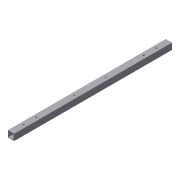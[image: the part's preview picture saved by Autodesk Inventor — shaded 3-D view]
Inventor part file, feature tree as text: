
AUTODESK INVENTOR PART (.ipt)
format: ipt  version: 2012 (Build 160160000, 160)  size: 108,544 bytes
history: native  units: in
note: dims shown in document units (in); Inventor stores cm internally (conversion verified against a paired STEP export)
features: extrude x3, sketch x3, shell x1
ambient origin geometry x8: Origin, YZ Plane, XZ Plane, XY Plane, X Axis, Y Axis, Z Axis, Center Point
bodies: Solid1 (feature_tree)
feature tree (7):
  extrude  "Extrusion1"  Depth=1.0in
  shell  "Shell1"  Thickness=25.0in
  extrude  "Extrusion2"  Depth=2.0in
  extrude  "Extrusion3"  Depth=0.5in
  sketch  "Sketch1"  dims[d0=1.0in d1=1.0in d2=25.0in d3=0.0in]
  sketch  "Sketch2"  dims[d4=0.125in d7=2.0in]
  sketch  "Sketch3"  dims[d8=2.0in d9=0.5in d10=0.5in d11=0.25in d12=0.25in d13=0.5in d14=0.5in d15=2.0in d16=2.0in d17=0.25in d18=0.25in d19=35.0in d20=0.0in d21=0.1875in d22=0.1875in d23=5.0in d24=10.0in d25=35.0in d26=0.0in]
